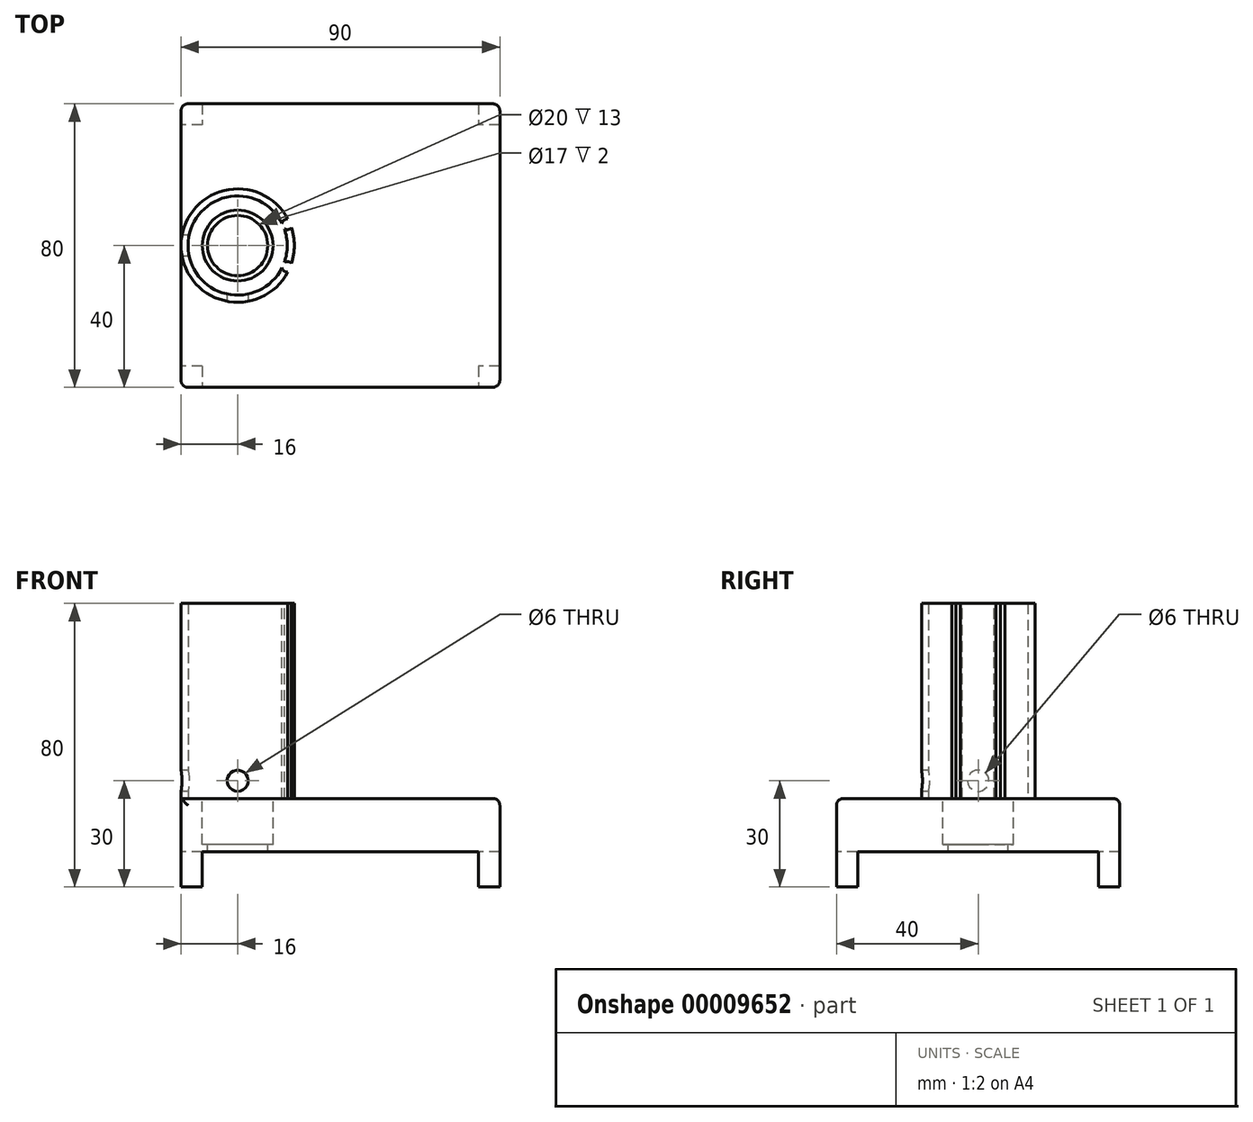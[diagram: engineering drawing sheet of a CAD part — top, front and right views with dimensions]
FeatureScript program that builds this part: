
annotation { "Feature Type Name" : "Feature", "Feature Type Description" : "" }
export const myFeature = defineFeature(function(context is Context, id is Id, definition is map)
    precondition{}
    {
        {
            var Q0;
            Q0=qCreatedBy(makeId("Top.planeOp"),FACE);
            var sketch = newSketch(context, id + "F0", { "sketchPlane" : qUnion([Q0])});
            skLineSegment(sketch, "E0.bottom", {"start": v(0, 0) * mm, "end": v(90, 0) * mm});
            skLineSegment(sketch, "E0.top", {"start": v(0, -80) * mm, "end": v(90, -80) * mm});
            skLineSegment(sketch, "E0.left", {"start": v(0, 0) * mm, "end": v(0, -80) * mm});
            skLineSegment(sketch, "E0.right", {"start": v(90, 0) * mm, "end": v(90, -80) * mm});
            skSolve(sketch);
        }
        {
            var Q0;
            Q0 = qSketchRegion(id + "F0", true);
            extrude(context, id + "F1", {"entities" : qUnion([Q0]), "depth" : 25 * mm});
        }
        {
            var Q0;
            Q0=makeQuery(id+"F1.opExtrude","CAP_FACE",FACE,{"disambiguationData":[OSD([sQuery(id+"F0.wireOp",EDGE,"E0.bottom"),sQuery(id+"F0.wireOp",EDGE,"E0.top"),sQuery(id+"F0.wireOp",EDGE,"E0.left"),sQuery(id+"F0.wireOp",EDGE,"E0.right")])],"isStart":false});
            var sketch = newSketch(context, id + "F2", { "sketchPlane" : qUnion([Q0])});
            skCircle(sketch, "E1", {"center": v(16, -40) * mm, "radius": 10 * mm});
            skLineSegment(sketch, "E2", {"start": v(0, -40) * mm, "end": v(80.38, -40) * mm, "construction": true});
            skSolve(sketch);
        }
        {
            var Q0;
            Q0 = qSketchRegion(id + "F2", true);
            extrude(context, id + "F3", {"entities" : qUnion([Q0]), "operationType" : NewBodyOperationType.REMOVE, "oppositeDirection" : true, "depth" : 13 * mm});
        }
        {
            var Q0;
            Q0=makeQuery(id+"F3.boolean.opBoolean","COPY",FACE,{"derivedFrom":makeQuery(id+"F3.opExtrude","CAP_FACE",FACE,{"disambiguationData":[OSD([sQuery(id+"F2.wireOp",EDGE,"E1")])],"isStart":false})});
            var sketch = newSketch(context, id + "F4", { "sketchPlane" : qUnion([Q0])});
            skCircle(sketch, "E3", {"center": v(16, -40) * mm, "radius": 8.5 * mm});
            skSolve(sketch);
        }
        {
            var Q0;
            Q0 = qSketchRegion(id + "F4", true);
            extrude(context, id + "F5", {"entities" : qUnion([Q0]), "operationType" : NewBodyOperationType.REMOVE, "oppositeDirection" : true, "depth" : 25 * mm});
        }
        {
            var Q0;
            Q0=makeQuery(id+"F1.opExtrude","SWEPT_FACE",FACE,{"disambiguationData":[OSD([sQuery(id+"F0.wireOp",EDGE,"E0.top")])]});
            var sketch = newSketch(context, id + "F6", { "sketchPlane" : qUnion([Q0])});
            skLineSegment(sketch, "E4", {"start": v(45, 0) * mm, "end": v(45, 25) * mm, "construction": true});
            skLineSegment(sketch, "E5.rect.bottom", {"start": v(84, 0) * mm, "end": v(6, 0) * mm});
            skLineSegment(sketch, "E5.rect.top", {"start": v(84, 10) * mm, "end": v(6, 10) * mm});
            skLineSegment(sketch, "E5.rect.left", {"start": v(84, 0) * mm, "end": v(84, 10) * mm});
            skLineSegment(sketch, "E5.rect.right", {"start": v(6, 0) * mm, "end": v(6, 10) * mm});
            skPoint(sketch, "E5.rect.middle", {"position": v(45, 5) * mm});
            skSolve(sketch);
        }
        {
            var Q0;
            Q0 = qSketchRegion(id + "F6", true);
            extrude(context, id + "F7", {"entities" : qUnion([Q0]), "operationType" : NewBodyOperationType.REMOVE, "endBound" : BoundingType.THROUGH_ALL, "oppositeDirection" : true, "depth" : 25 * mm});
        }
        {
            var Q0;
            Q0=makeQuery(id+"F1.opExtrude","SWEPT_FACE",FACE,{"disambiguationData":[OSD([sQuery(id+"F0.wireOp",EDGE,"E0.left")])]});
            var sketch = newSketch(context, id + "F8", { "sketchPlane" : qUnion([Q0])});
            skLineSegment(sketch, "E6", {"start": v(40, 25) * mm, "end": v(40, 0) * mm, "construction": true});
            skLineSegment(sketch, "E7.rect.bottom", {"start": v(74, 0) * mm, "end": v(6, 0) * mm});
            skLineSegment(sketch, "E7.rect.top", {"start": v(74, 10) * mm, "end": v(6, 10) * mm});
            skLineSegment(sketch, "E7.rect.left", {"start": v(74, 0) * mm, "end": v(74, 10) * mm});
            skLineSegment(sketch, "E7.rect.right", {"start": v(6, 0) * mm, "end": v(6, 10) * mm});
            skPoint(sketch, "E7.rect.middle", {"position": v(40, 5) * mm});
            skSolve(sketch);
        }
        {
            var Q0;
            Q0 = qSketchRegion(id + "F8", true);
            extrude(context, id + "F9", {"entities" : qUnion([Q0]), "operationType" : NewBodyOperationType.REMOVE, "endBound" : BoundingType.THROUGH_ALL, "oppositeDirection" : true, "depth" : 25 * mm});
        }
        {
            var Q0;
            Q0=makeQuery(id+"F1.opExtrude","CAP_FACE",FACE,{"disambiguationData":[OSD([sQuery(id+"F0.wireOp",EDGE,"E0.bottom"),sQuery(id+"F0.wireOp",EDGE,"E0.top"),sQuery(id+"F0.wireOp",EDGE,"E0.left"),sQuery(id+"F0.wireOp",EDGE,"E0.right")])],"isStart":false});
            var sketch = newSketch(context, id + "F10", { "sketchPlane" : qUnion([Q0])});
            skCircle(sketch, "E8", {"center": v(16, -40) * mm, "radius": 16 * mm});
            skCircle(sketch, "E9", {"center": v(16, -40) * mm, "radius": 14 * mm});
            skSolve(sketch);
        }
        {
            var Q0;
            Q0 = qSketchRegion(id + "F10", true);
            extrude(context, id + "F11", {"entities" : qUnion([Q0]), "operationType" : NewBodyOperationType.ADD, "depth" : 55 * mm});
        }
        {
            var Q0;
            Q0=makeQuery(id+"F1.opExtrude","SWEPT_FACE",FACE,{"disambiguationData":[OSD([sQuery(id+"F0.wireOp",EDGE,"E0.left")])]});
            var sketch = newSketch(context, id + "F12", { "sketchPlane" : qUnion([Q0])});
            skLineSegment(sketch, "E10", {"start": v(40, 10) * mm, "end": v(40, 45.6) * mm, "construction": true});
            skCircle(sketch, "E11", {"center": v(40, 30) * mm, "radius": 3 * mm});
            skSolve(sketch);
        }
        {
            var Q0;
            Q0 = qSketchRegion(id + "F12", true);
            extrude(context, id + "F13", {"entities" : qUnion([Q0]), "operationType" : NewBodyOperationType.REMOVE, "oppositeDirection" : true, "depth" : 5 * mm});
        }
        {
            var Q0;
            Q0=makeQuery(id+"F1.opExtrude","SWEPT_FACE",FACE,{"disambiguationData":[OSD([sQuery(id+"F0.wireOp",EDGE,"E0.top")])]});
            var sketch = newSketch(context, id + "F14", { "sketchPlane" : qUnion([Q0])});
            skLineSegment(sketch, "E12", {"start": v(16, 10) * mm, "end": v(16, 48.3) * mm, "construction": true});
            skCircle(sketch, "E13", {"center": v(16, 30) * mm, "radius": 3 * mm});
            skSolve(sketch);
        }
        {
            var Q0;
            Q0=makeQuery(id+"F14.imprint","IMPRINT",FACE,{"disambiguationData":[TD([[makeQuery(id+"F14.imprint","IMPRINT",EDGE,{"derivedFrom":sQuery(id+"F14.wireOp",EDGE,"E13")}),1.0]])]});
            extrude(context, id + "F15", {"entities" : qUnion([Q0]), "operationType" : NewBodyOperationType.REMOVE, "oppositeDirection" : true, "depth" : 40 * mm});
        }
        {
            var Q0;
            Q0=makeQuery(id+"F11.opExtrude","CAP_FACE",FACE,{"disambiguationData":[OSD([sQuery(id+"F10.wireOp",EDGE,"E8"),sQuery(id+"F10.wireOp",EDGE,"E9")])],"isStart":false});
            var sketch = newSketch(context, id + "F16", { "sketchPlane" : qUnion([Q0])});
            skLineSegment(sketch, "E14", {"start": v(0, -40) * mm, "end": v(38.22, -40) * mm, "construction": true});
            skCircle(sketch, "E15", {"center": v(30, -46) * mm, "radius": 1.5 * mm});
            skCircle(sketch, "E16", {"center": v(30, -34) * mm, "radius": 1.5 * mm});
            skLineSegment(sketch, "E17", {"start": v(16, -40) * mm, "end": v(16, -18.14) * mm, "construction": true});
            skSolve(sketch);
        }
        {
            var Q0;
            Q0 = qSketchRegion(id + "F16", true);
            extrude(context, id + "F17", {"entities" : qUnion([Q0]), "operationType" : NewBodyOperationType.REMOVE, "oppositeDirection" : true, "depth" : 55 * mm});
        }
        {
            var Q0;
            Q0=makeQuery(id+"F1.opExtrude","CAP_EDGE",EDGE,{"disambiguationData":[OSD([sQuery(id+"F0.wireOp",EDGE,"E0.right")])],"isStart":false});
            var Q1;
            Q1=makeQuery(id+"F1.opExtrude","CAP_EDGE",EDGE,{"disambiguationData":[OSD([sQuery(id+"F0.wireOp",EDGE,"E0.bottom")])],"isStart":false});
            var Q2;
            Q2=makeQuery(id+"F1.opExtrude","CAP_EDGE",EDGE,{"disambiguationData":[OSD([sQuery(id+"F0.wireOp",EDGE,"E0.top")])],"isStart":false});
            var Q3;
            Q3=makeQuery(id+"F1.opExtrude","SWEPT_EDGE",EDGE,{"disambiguationData":[OSD([sQuery(id+"F0.wireOp",EDGE,"E0.top"),sQuery(id+"F0.wireOp",EDGE,"E0.left")])]});
            var Q4;
            Q4=makeQuery(id+"F1.opExtrude","SWEPT_EDGE",EDGE,{"disambiguationData":[OSD([sQuery(id+"F0.wireOp",EDGE,"E0.bottom"),sQuery(id+"F0.wireOp",EDGE,"E0.left")])]});
            var Q5;
            Q5=makeQuery(id+"F1.opExtrude","SWEPT_EDGE",EDGE,{"disambiguationData":[OSD([sQuery(id+"F0.wireOp",EDGE,"E0.bottom"),sQuery(id+"F0.wireOp",EDGE,"E0.right")])]});
            var Q6;
            Q6=makeQuery(id+"F1.opExtrude","SWEPT_EDGE",EDGE,{"disambiguationData":[OSD([sQuery(id+"F0.wireOp",EDGE,"E0.top"),sQuery(id+"F0.wireOp",EDGE,"E0.right")])]});
            fillet(context, id + "F18", {"entities" : qUnion([Q0, Q1, Q2, Q3, Q4, Q5, Q6]), "radius" : 2 * mm, "tangentPropagation" : true, "allowEdgeOverflow" : false});
        }
    });
